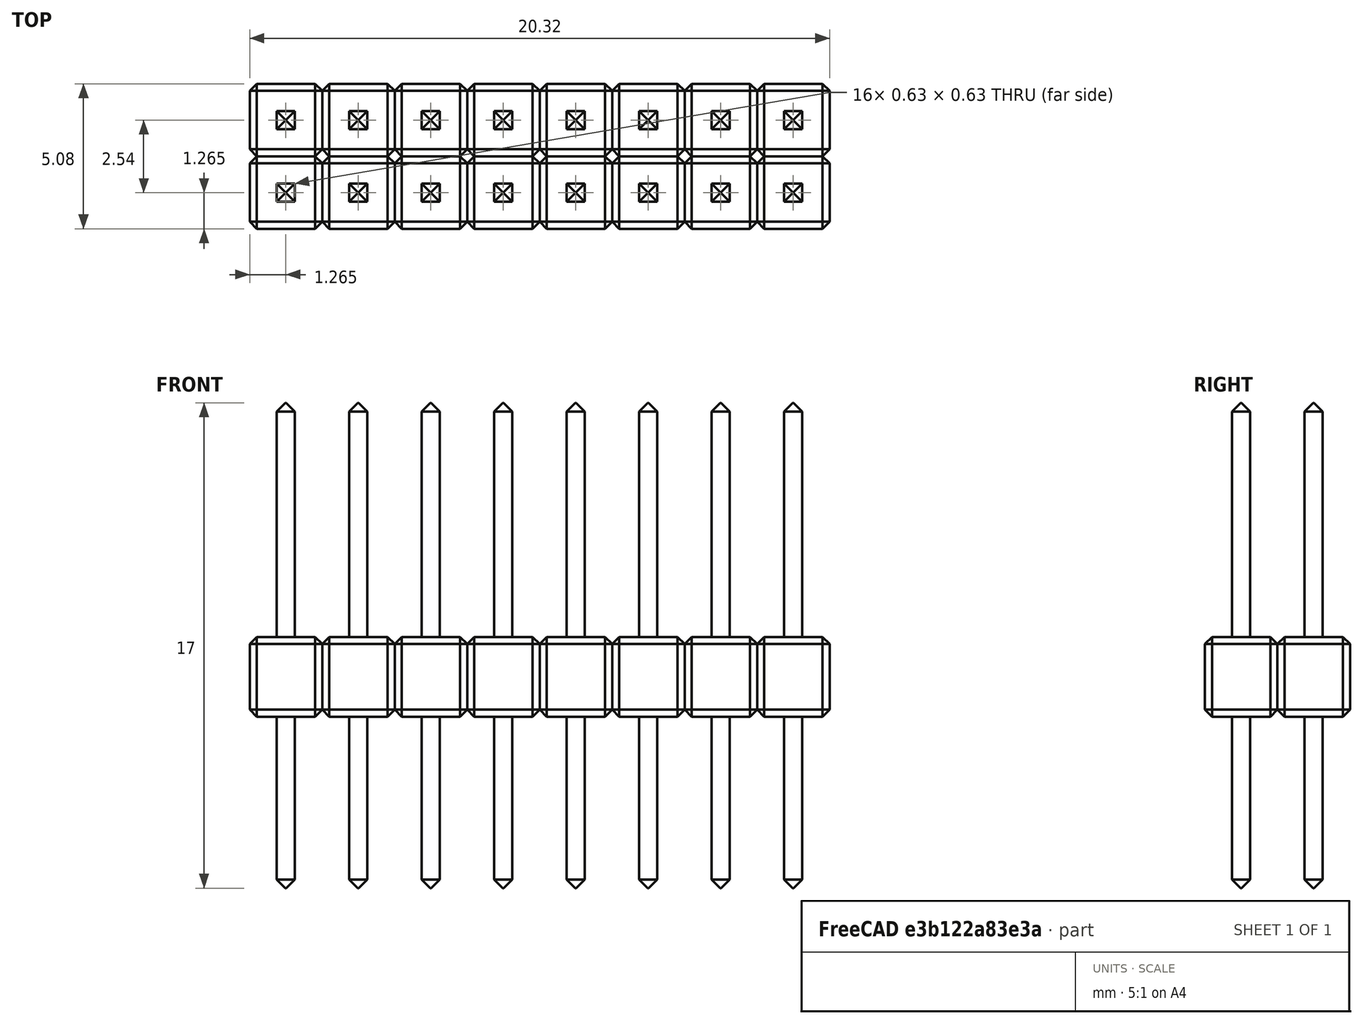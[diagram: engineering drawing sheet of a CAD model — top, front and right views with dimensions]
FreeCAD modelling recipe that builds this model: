
FCSTD DOCUMENT  (FreeCAD 0.18R4 (GitTag))
Label: 16 Pin Header Dual Row
License: All rights reserved
LicenseURL: http://en.wikipedia.org/wiki/All_rights_reserved
objects: Part::Box×2, Part::Chamfer×2, Part::FeaturePython×2, Part::MultiFuse×1
note: 7 computed .brp shape members not serialized (recipe doc carries the construction recipe); baked Part::Feature solids carry a one-line shape summary decoded from their .brp

FEATURE [Part::Box] Box  label="Cube"
  AttacherType = Attacher::AttachEngine3D
  Height = 2.8
  Length = 2.54
  Width = 2.54
FEATURE [Part::Chamfer] Chamfer  label="Body"
  Base = -> Box
  Edges = 12 edges r=0.25: [Edge1,Edge2,Edge3,Edge4,Edge5,Edge6,Edge7,Edge8,Edge9,Edge10,Edge11,Edge12]
FEATURE [Part::Box] Box001  label="Cube001"
  AttacherType = Attacher::AttachEngine3D
  Height = 17
  Length = 0.63
  Placement = pos=(-3,0,0) rot=(0,0,1;0rad)
  Width = 0.63
FEATURE [Part::Chamfer] Chamfer001  label="Pin"
  Base = -> Box001
  Edges = 8 edges r=0.3: [Edge2,Edge4,Edge6,Edge8,Edge9,Edge10,Edge11,Edge12]
  Placement = pos=(3.95,0.95,-6) rot=(0,0,1;0rad)
FEATURE [Part::FeaturePython] Array  label="Bodies"  # Draft array (typed FeaturePython)
  Angle = 360
  ArrayType = 0
  Axis = (0,0,1)
  Base = -> Chamfer
  Center = (0,0,0)
  Fuse = false
  IntervalAxis = (0,0,0)
  IntervalX = (2.54,0,0)
  IntervalY = (0,2.54,0)
  IntervalZ = (0,0,1)
  NumberPolar = 1
  NumberX = 8
  NumberY = 2
  NumberZ = 1
FEATURE [Part::FeaturePython] Array001  label="Pins"  # Draft array (typed FeaturePython)
  Angle = 360
  ArrayType = 0
  Axis = (0,0,1)
  Base = -> Chamfer001
  Center = (0,0,0)
  Fuse = false
  IntervalAxis = (0,0,0)
  IntervalX = (2.54,0,0)
  IntervalY = (0,2.54,0)
  IntervalZ = (0,0,1)
  NumberPolar = 1
  NumberX = 8
  NumberY = 2
  NumberZ = 1
FEATURE [Part::MultiFuse] Fusion  label="Header"
  Shapes = -> [Array,Array001]
